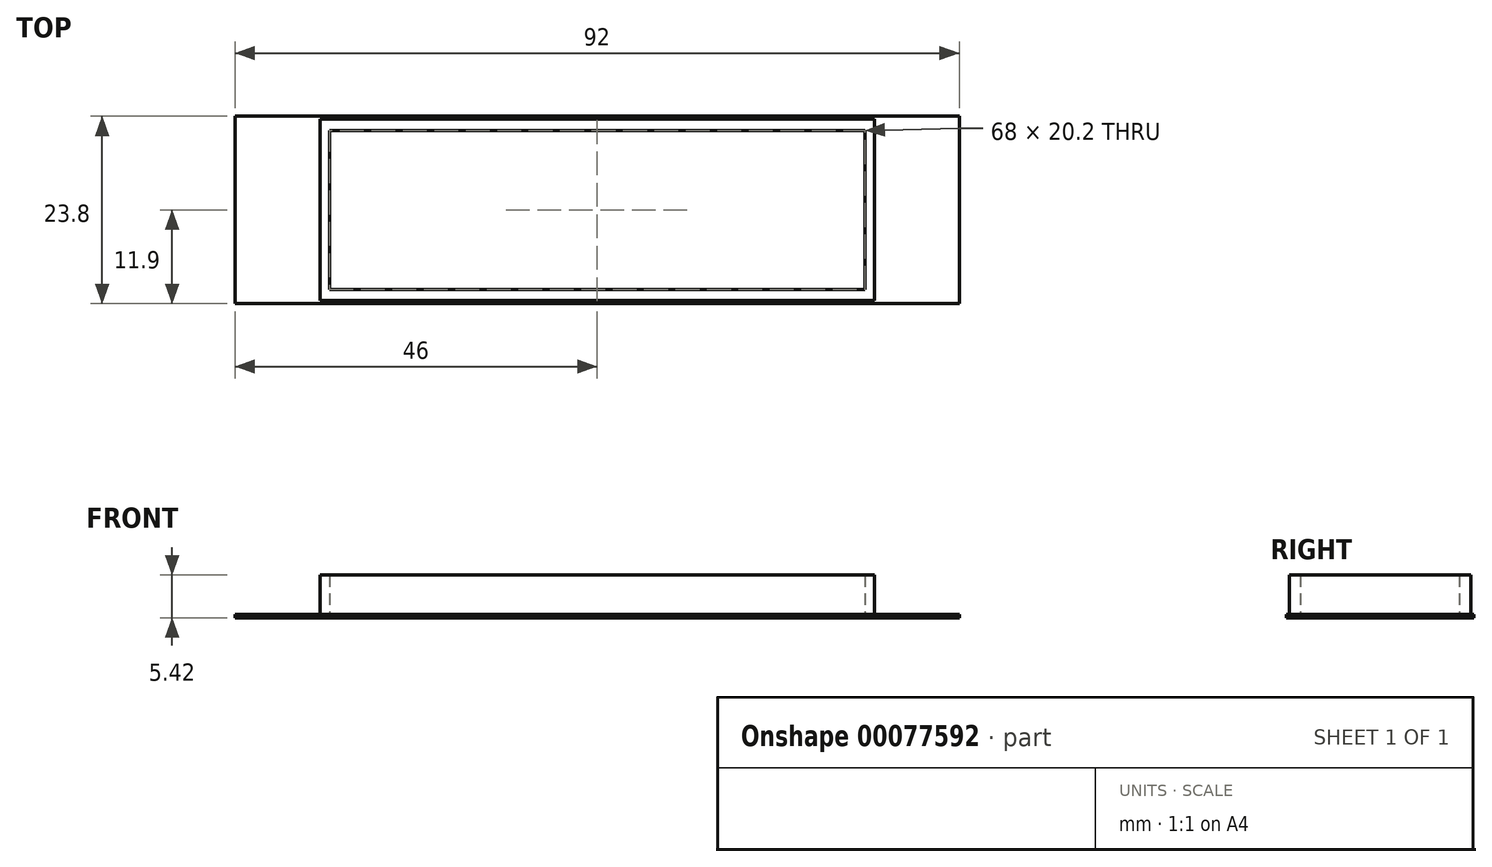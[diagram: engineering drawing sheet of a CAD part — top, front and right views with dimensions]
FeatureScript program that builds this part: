
annotation { "Feature Type Name" : "Feature", "Feature Type Description" : "" }
export const myFeature = defineFeature(function(context is Context, id is Id, definition is map)
    precondition{}
    {
        {
            var Q0;
            Q0=qCreatedBy(makeId("Top.planeOp"),FACE);
            var sketch = newSketch(context, id + "F0", { "sketchPlane" : qUnion([Q0])});
            skLineSegment(sketch, "E0.bottom", {"start": v(-46, 11.9) * mm, "end": v(46, 11.9) * mm});
            skLineSegment(sketch, "E0.top", {"start": v(-46, -11.9) * mm, "end": v(46, -11.9) * mm});
            skLineSegment(sketch, "E0.left", {"start": v(-46, 11.9) * mm, "end": v(-46, -11.9) * mm});
            skLineSegment(sketch, "E0.right", {"start": v(46, 11.9) * mm, "end": v(46, -11.9) * mm});
            skLineSegment(sketch, "E1", {"start": v(-46, 11.9) * mm, "end": v(46, -11.9) * mm, "construction": true});
            skSolve(sketch);
        }
        {
            var Q0;
            Q0=makeQuery(id+"F0.imprint","IMPRINT",FACE,{"disambiguationData":[TD([[makeQuery(id+"F0.imprint","IMPRINT",EDGE,{"derivedFrom":sQuery(id+"F0.wireOp",EDGE,"E0.bottom")}),-1.0]])]});
            extrude(context, id + "F1", {"entities" : qUnion([Q0]), "depth" : 0.42 * mm});
        }
        {
            var Q0;
            Q0=makeQuery(id+"F1.opExtrude","CAP_FACE",FACE,{"disambiguationData":[OSD([sQuery(id+"F0.wireOp",EDGE,"E0.bottom"),sQuery(id+"F0.wireOp",EDGE,"E0.top"),sQuery(id+"F0.wireOp",EDGE,"E0.left"),sQuery(id+"F0.wireOp",EDGE,"E0.right")])],"isStart":false});
            var sketch = newSketch(context, id + "F2", { "sketchPlane" : qUnion([Q0])});
            skLineSegment(sketch, "E2.top", {"start": v(-35.05, -11.9) * mm, "end": v(35.05, -11.9) * mm});
            skPoint(sketch, "E2.middle", {"position": v(0, 0) * mm});
            skLineSegment(sketch, "E3.bottom", {"start": v(-35.2, 11.5) * mm, "end": v(35.2, 11.5) * mm});
            skLineSegment(sketch, "E3.top", {"start": v(-35.2, -11.5) * mm, "end": v(35.2, -11.5) * mm});
            skLineSegment(sketch, "E3.left", {"start": v(-35.2, 11.5) * mm, "end": v(-35.2, -11.5) * mm});
            skLineSegment(sketch, "E3.right", {"start": v(35.2, 11.5) * mm, "end": v(35.2, -11.5) * mm});
            skLineSegment(sketch, "E4.bottom", {"start": v(-34, 10.1) * mm, "end": v(34, 10.1) * mm});
            skLineSegment(sketch, "E4.top", {"start": v(-34, -10.1) * mm, "end": v(34, -10.1) * mm});
            skLineSegment(sketch, "E4.left", {"start": v(-34, 10.1) * mm, "end": v(-34, -10.1) * mm});
            skLineSegment(sketch, "E4.right", {"start": v(34, 10.1) * mm, "end": v(34, -10.1) * mm});
            skSolve(sketch);
        }
        {
            var Q0;
            Q0 = qSketchRegion(id + "F2", true);
            extrude(context, id + "F3", {"entities" : qUnion([Q0]), "operationType" : NewBodyOperationType.ADD, "depth" : 5 * mm});
        }
        {
            var Q0;
            Q0=makeQuery(id+"F3.boolean.opBoolean","SPLIT",FACE,{"disambiguationData":[TD([makeQuery(id+"F3.opExtrude","SWEPT_FACE",FACE,{"disambiguationData":[OSD([sQuery(id+"F2.wireOp",EDGE,"E4.bottom")])]})])],"derivedFrom":makeQuery(id+"F1.opExtrude","CAP_FACE",FACE,{"disambiguationData":[OSD([sQuery(id+"F0.wireOp",EDGE,"E0.bottom"),sQuery(id+"F0.wireOp",EDGE,"E0.top"),sQuery(id+"F0.wireOp",EDGE,"E0.left"),sQuery(id+"F0.wireOp",EDGE,"E0.right")])],"isStart":false})});
            var sketch = newSketch(context, id + "F4", { "sketchPlane" : qUnion([Q0])});
            skLineSegment(sketch, "E5.bottom", {"start": v(-34, 10.1) * mm, "end": v(34, 10.1) * mm});
            skLineSegment(sketch, "E5.top", {"start": v(-34, -10.1) * mm, "end": v(34, -10.1) * mm});
            skLineSegment(sketch, "E5.left", {"start": v(-34, 10.1) * mm, "end": v(-34, -10.1) * mm});
            skLineSegment(sketch, "E5.right", {"start": v(34, 10.1) * mm, "end": v(34, -10.1) * mm});
            skSolve(sketch);
        }
        {
            var Q0;
            Q0 = qSketchRegion(id + "F4", true);
            extrude(context, id + "F5", {"entities" : qUnion([Q0]), "operationType" : NewBodyOperationType.REMOVE, "oppositeDirection" : true, "depth" : 25 * mm});
        }
    });
